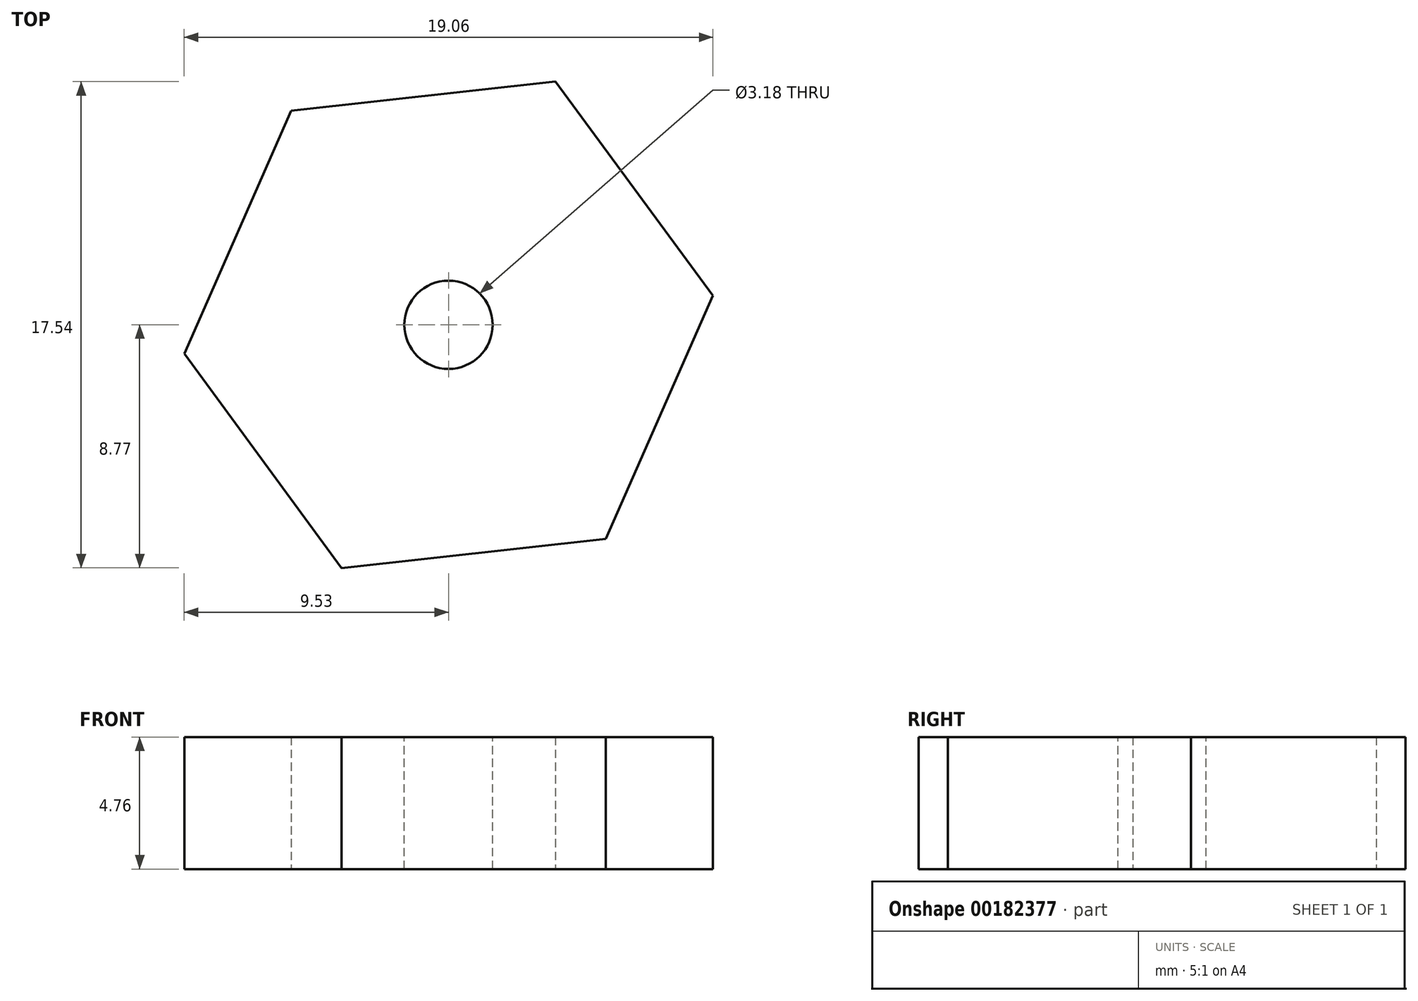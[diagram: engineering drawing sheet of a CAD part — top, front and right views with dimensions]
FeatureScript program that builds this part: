
annotation { "Feature Type Name" : "Feature", "Feature Type Description" : "" }
export const myFeature = defineFeature(function(context is Context, id is Id, definition is map)
    precondition{}
    {
        {
            var Q0;
            Q0=qCreatedBy(makeId("Top.planeOp"),FACE);
            var sketch = newSketch(context, id + "F0", { "sketchPlane" : qUnion([Q0])});
            skCircle(sketch, "E0.cCircle", {"center": v(0, 0) * mm, "radius": 8.3 * mm, "construction": true});
            skLineSegment(sketch, "E0.0", {"start": v(-3.86, -8.77) * mm, "end": v(-9.52, -1.05) * mm});
            skLineSegment(sketch, "E0.1", {"start": v(-9.52, -1.05) * mm, "end": v(-5.67, 7.73) * mm});
            skLineSegment(sketch, "E0.2", {"start": v(-5.67, 7.73) * mm, "end": v(3.86, 8.77) * mm});
            skLineSegment(sketch, "E0.3", {"start": v(3.86, 8.77) * mm, "end": v(9.52, 1.05) * mm});
            skLineSegment(sketch, "E0.4", {"start": v(9.52, 1.05) * mm, "end": v(5.67, -7.73) * mm});
            skLineSegment(sketch, "E0.5", {"start": v(5.67, -7.73) * mm, "end": v(-3.86, -8.77) * mm});
            skPoint(sketch, "E0.0.midPoint", {"position": v(-6.7, -4.91) * mm});
            skSolve(sketch);
        }
        {
            var Q0;
            Q0 = qSketchRegion(id + "F0", true);
            extrude(context, id + "F1", {"entities" : qUnion([Q0]), "depth" : 4.76 * mm});
        }
        {
            var Q0;
            Q0=makeQuery(id+"F1.opExtrude","CAP_FACE",FACE,{"disambiguationData":[OSD([sQuery(id+"F0.wireOp",EDGE,"E0.0"),sQuery(id+"F0.wireOp",EDGE,"E0.1"),sQuery(id+"F0.wireOp",EDGE,"E0.2"),sQuery(id+"F0.wireOp",EDGE,"E0.3"),sQuery(id+"F0.wireOp",EDGE,"E0.4"),sQuery(id+"F0.wireOp",EDGE,"E0.5")])],"isStart":false});
            var sketch = newSketch(context, id + "F2", { "sketchPlane" : qUnion([Q0])});
            skCircle(sketch, "E1", {"center": v(0, 0) * mm, "radius": 1.6 * mm});
            skSolve(sketch);
        }
        {
            var Q0;
            Q0 = qSketchRegion(id + "F2", true);
            extrude(context, id + "F3", {"entities" : qUnion([Q0]), "operationType" : NewBodyOperationType.REMOVE, "oppositeDirection" : true, "depth" : 9.52 * mm});
        }
    });
